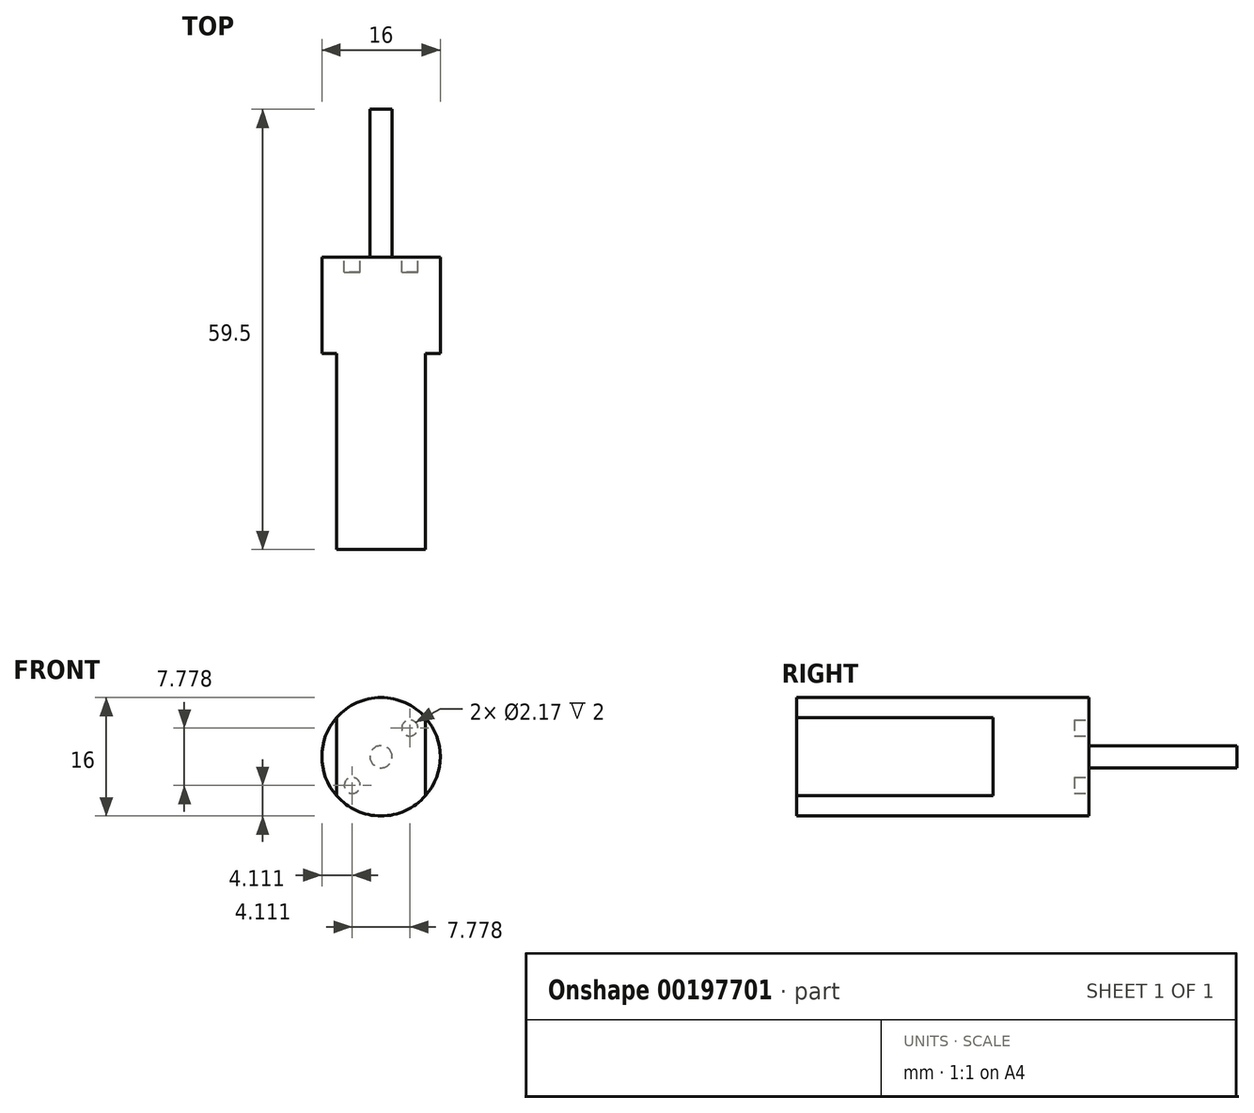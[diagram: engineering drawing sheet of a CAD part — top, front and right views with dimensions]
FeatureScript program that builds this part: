
annotation { "Feature Type Name" : "Feature", "Feature Type Description" : "" }
export const myFeature = defineFeature(function(context is Context, id is Id, definition is map)
    precondition{}
    {
        {
            var Q0;
            Q0=qCreatedBy(makeId("Front.planeOp"),FACE);
            var sketch = newSketch(context, id + "F0", { "sketchPlane" : qUnion([Q0])});
            skCircle(sketch, "E0", {"center": v(0, 0) * mm, "radius": 8 * mm});
            skSolve(sketch);
        }
        {
            var Q0;
            Q0 = qSketchRegion(id + "F0", true);
            extrude(context, id + "F1", {"entities" : qUnion([Q0]), "depth" : 13 * mm});
        }
        {
            var Q0;
            Q0=makeQuery(id+"F1.opExtrude","CAP_FACE",FACE,{"disambiguationData":[OSD([sQuery(id+"F0.wireOp",EDGE,"E0")])],"isStart":false});
            var sketch = newSketch(context, id + "F2", { "sketchPlane" : qUnion([Q0])});
            skLineSegment(sketch, "E1", {"start": v(0, 0) * mm, "end": v(0, 22.85) * mm, "construction": true});
            skLineSegment(sketch, "E2", {"start": v(-6, 5.3) * mm, "end": v(-6, -5.3) * mm});
            skLineSegment(sketch, "E3", {"start": v(6, 5.3) * mm, "end": v(6, -5.3) * mm});
            skArc(sketch, "E4", {"start": v(-6, 5.3) * mm, "mid": v(0, 8) * mm, "end": v(6, 5.3) * mm});
            skArc(sketch, "E5", {"start": v(6, -5.3) * mm, "mid": v(0, -8) * mm, "end": v(-6, -5.3) * mm});
            skSolve(sketch);
        }
        {
            var Q0;
            Q0 = qSketchRegion(id + "F2", true);
            extrude(context, id + "F3", {"entities" : qUnion([Q0]), "operationType" : NewBodyOperationType.ADD, "depth" : 26.5 * mm});
        }
        {
            var Q0;
            Q0=makeQuery(id+"F1.opExtrude","CAP_FACE",FACE,{"disambiguationData":[OSD([sQuery(id+"F0.wireOp",EDGE,"E0")])],"isStart":true});
            var sketch = newSketch(context, id + "F4", { "sketchPlane" : qUnion([Q0])});
            skCircle(sketch, "E6", {"center": v(0, 0) * mm, "radius": 1.5 * mm});
            skSolve(sketch);
        }
        {
            var Q0;
            Q0 = qSketchRegion(id + "F4", true);
            extrude(context, id + "F5", {"entities" : qUnion([Q0]), "operationType" : NewBodyOperationType.ADD, "depth" : 20 * mm});
        }
        {
            var Q0;
            Q0=makeQuery(id+"F1.opExtrude","CAP_FACE",FACE,{"disambiguationData":[OSD([sQuery(id+"F0.wireOp",EDGE,"E0")])],"isStart":true});
            var sketch = newSketch(context, id + "F6", { "sketchPlane" : qUnion([Q0])});
            skLineSegment(sketch, "E7", {"start": v(0, 0) * mm, "end": v(5.66, -5.66) * mm, "construction": true});
            skCircle(sketch, "E8", {"center": v(3.89, -3.89) * mm, "radius": 1.08 * mm});
            skCircle(sketch, "E9.1.0", {"center": v(-3.89, 3.89) * mm, "radius": 1.08 * mm});
            skPoint(sketch, "E9.center", {"position": v(0, 0) * mm});
            skLineSegment(sketch, "E10", {"start": v(0, 0) * mm, "end": v(0, 8) * mm, "construction": true});
            skSolve(sketch);
        }
        {
            var Q0;
            Q0 = qSketchRegion(id + "F6", true);
            extrude(context, id + "F7", {"entities" : qUnion([Q0]), "operationType" : NewBodyOperationType.REMOVE, "oppositeDirection" : true, "depth" : 2 * mm});
        }
    });
